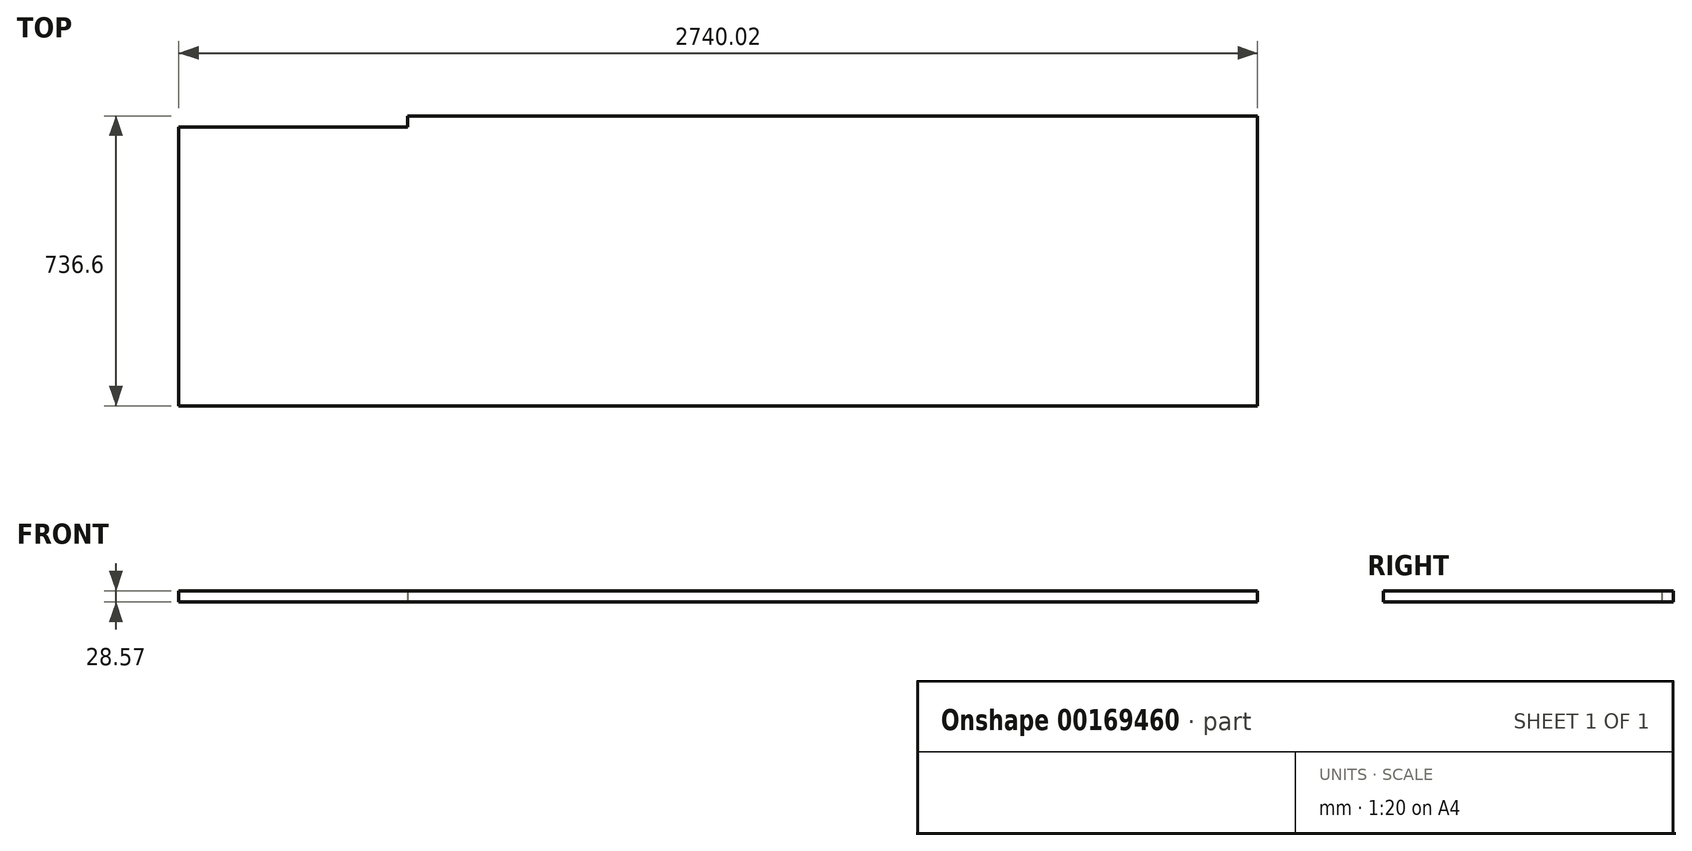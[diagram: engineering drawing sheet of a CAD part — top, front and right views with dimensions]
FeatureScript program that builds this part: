
annotation { "Feature Type Name" : "Feature", "Feature Type Description" : "" }
export const myFeature = defineFeature(function(context is Context, id is Id, definition is map)
    precondition{}
    {
        {
            var Q0;
            Q0=qCreatedBy(makeId("Top.planeOp"),FACE);
            var sketch = newSketch(context, id + "F0", { "sketchPlane" : qUnion([Q0])});
            skLineSegment(sketch, "E0", {"start": v(-1350.34, 502.93) * mm, "end": v(-769.32, 502.93) * mm});
            skLineSegment(sketch, "E1", {"start": v(-769.32, 502.93) * mm, "end": v(-769.32, 531.5) * mm});
            skLineSegment(sketch, "E2", {"start": v(-769.32, 531.5) * mm, "end": v(1389.68, 531.5) * mm});
            skLineSegment(sketch, "E3", {"start": v(1389.68, 531.5) * mm, "end": v(1389.68, -205.1) * mm});
            skLineSegment(sketch, "E4", {"start": v(1389.68, -205.1) * mm, "end": v(-1350.34, -205.1) * mm});
            skLineSegment(sketch, "E5", {"start": v(-1350.34, 502.93) * mm, "end": v(-1350.34, -205.1) * mm});
            skSolve(sketch);
        }
        {
            var Q0;
            Q0 = qSketchRegion(id + "F0", true);
            extrude(context, id + "F1", {"entities" : qUnion([Q0]), "depth" : 28.57 * mm});
        }
    });
